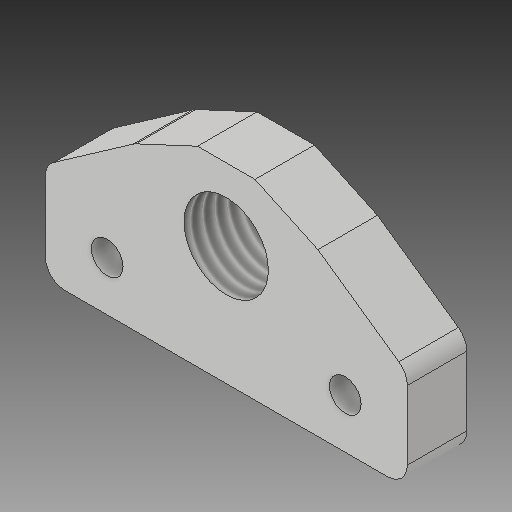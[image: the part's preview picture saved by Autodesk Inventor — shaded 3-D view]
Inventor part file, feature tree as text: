
AUTODESK INVENTOR PART (.ipt)
format: ipt  version: 2018 (Build 220112000, 112)  size: 133,120 bytes
history: native  units: mm
features: other x3, sketch x1
ambient origin geometry x8: Origin, YZ Plane, XZ Plane, XY Plane, X Axis, Y Axis, Z Axis, Center Point
bodies: Solid1 (feature_tree)
feature tree (4):
  other  "pshfit-mount-acrylic_MIR.ipt"
  other  "Solid1::pshfit-mount-acrylic_MIR.ipt"
  other  "TaggingFeature1"
  sketch  "Sketch1"  dims[d0=10.0mm]
